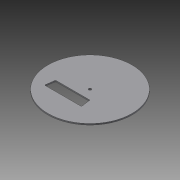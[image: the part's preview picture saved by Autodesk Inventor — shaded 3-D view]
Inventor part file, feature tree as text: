
AUTODESK INVENTOR PART (.ipt)
format: ipt  version: 2015 (Build 190159000, 159)  size: 100,352 bytes
history: native  units: mm
features: extrude x2, chamfer x2, sketch x2, fillet x1
ambient origin geometry x8: Origin, YZ Plane, XZ Plane, XY Plane, X Axis, Y Axis, Z Axis, Center Point
bodies: Solid1 (feature_tree)
feature tree (7):
  extrude  "Extrusion1"  Depth=94.0mm
  extrude  "Extrusion2"  Depth=1.0mm
  chamfer  "Chamfer1"  Distance=11.0mm
  chamfer  "Chamfer2"  Distance=9.0mm
  fillet  "Fillet1"  Radius=12.0mm
  sketch  "Sketch1"  dims[d0=3.0mm d1=94.0mm]
  sketch  "Sketch2"  dims[d2=1.5mm d3=0.0mm d4=41.5mm d5=11.0mm d6=9.0mm d7=12.0mm d8=1.5mm d9=0.0mm d10=11.0mm d11=1.5mm d12=45.0deg d13=11.0mm d14=1.5mm d15=45.0deg d16=1.0mm]
